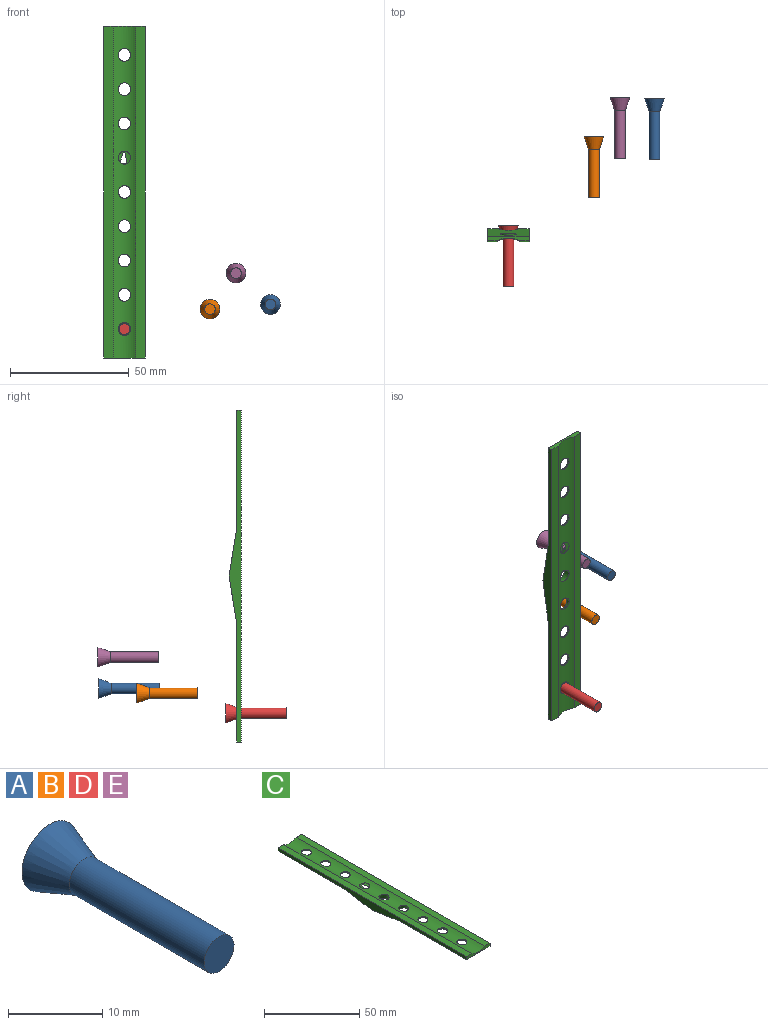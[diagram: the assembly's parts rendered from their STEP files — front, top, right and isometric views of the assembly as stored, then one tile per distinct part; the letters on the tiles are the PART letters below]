
ASSEMBLY  parts=5 mates=1
PART A: 4 faces, bbox 8.3x25.5x8.3 mm
  f0: plane 4.5x4.5mm, normal (0,-1,0), area 15.9mm2, adj f1
  f1: cylinder r=2.25mm len=20.3mm, axis (0,-1,0), area 287mm2, adj f0,f2
  f2: cone r=4.14mm half-angle=20deg, axis (0,1,0), area 111.1mm2, adj f1,f3
  f3: plane 8.29x8.29mm, normal (0,1,0), area 53.9mm2, adj f2
PART B: same geometry as A
PART C: 20 faces, bbox 17.6x140.1x5.3 mm
  f0: plane 140x4mm, normal (0,0,1), area 559.4mm2, adj f1,f2,f3,f19
  f1: plane 140x5.2mm, normal (1,0,0), area 344mm2, adj f0,f2,f3,f15,f16,f17,f18
  f2: plane 17.5x2mm, normal (0,1,0), area 27mm2, adj f0,f1,f4,f10,f17,f19
  f3: plane 17.5x2mm, normal (0,-1,0), area 27mm2, adj f0,f1,f4,f10,f15,f19
  f4: plane 140x5.2mm, normal (-1,0,0), area 344mm2, adj f2,f3,f10,f15,f16,f17,f18
  f5: cone r=2.25mm half-angle=20deg, axis (0,0,-1), area 17.4mm2, adj f15,f19
  f6: cone r=2.25mm half-angle=20deg, axis (0,0,-1), area 17.4mm2, adj f15,f19
  f7: cone r=2.25mm half-angle=20deg, axis (0,0,-1), area 17.4mm2, adj f15,f19
  f8: cone r=2.25mm half-angle=20deg, axis (0,0,-1), area 36.6mm2, adj f16,f19
  f9: cone r=2.25mm half-angle=20deg, axis (0,0,-1), area 82.6mm2, adj f16,f18,f19
  f10: plane 140x4mm, normal (0,0,1), area 559.4mm2, adj f2,f3,f4,f19
  f11: cone r=2.25mm half-angle=20deg, axis (0,0,-1), area 36.5mm2, adj f18,f19
  f12: cone r=2.25mm half-angle=20deg, axis (0,0,-1), area 17.4mm2, adj f17,f19
  f13: cone r=2.25mm half-angle=20deg, axis (0,0,-1), area 17.4mm2, adj f17,f19
  f14: cone r=2.25mm half-angle=20deg, axis (0,0,-1), area 17.4mm2, adj f17,f19
  f15: plane 50x17.5mm, normal (0,0,-1), area 791.4mm2, adj f1,f3,f4,f5,f6,f7,f16
  f16: plane 20x17.5mm, normal (0,-0.16,-0.99), area 294.2mm2, adj f1,f4,f8,f9,f15,f18
  f17: plane 50x17.5mm, normal (0,0,-1), area 791.4mm2, adj f1,f2,f4,f12,f13,f14,f18
  f18: plane 20.08x17.58mm, normal (0,0.16,-0.99), area 294.2mm2, adj f1,f4,f9,f11,f16,f17
  f19: cylinder r=9.66mm len=140mm, axis (0,-1,0), area 1192.8mm2, adj f0,f2,f3,f5,f6,f7,f8,f9
PART D: same geometry as A
PART E: same geometry as A
PLACE A t=(-4.86,-41.58,-39.04)mm
PLACE B t=(-30.39,-57.63,-41.01)mm
PLACE C rot(axis=(1,0,0),90deg) t=(-75.22,-71.01,78.4)mm
PLACE D t=(-66.47,-95.06,-49.4)mm
PLACE E t=(-19.41,-41.16,-25.81)mm
MATE revolute C.f5 <-> D.f1  axis (0,1,0) through (-66.47,-74.76,-49.4)mm
